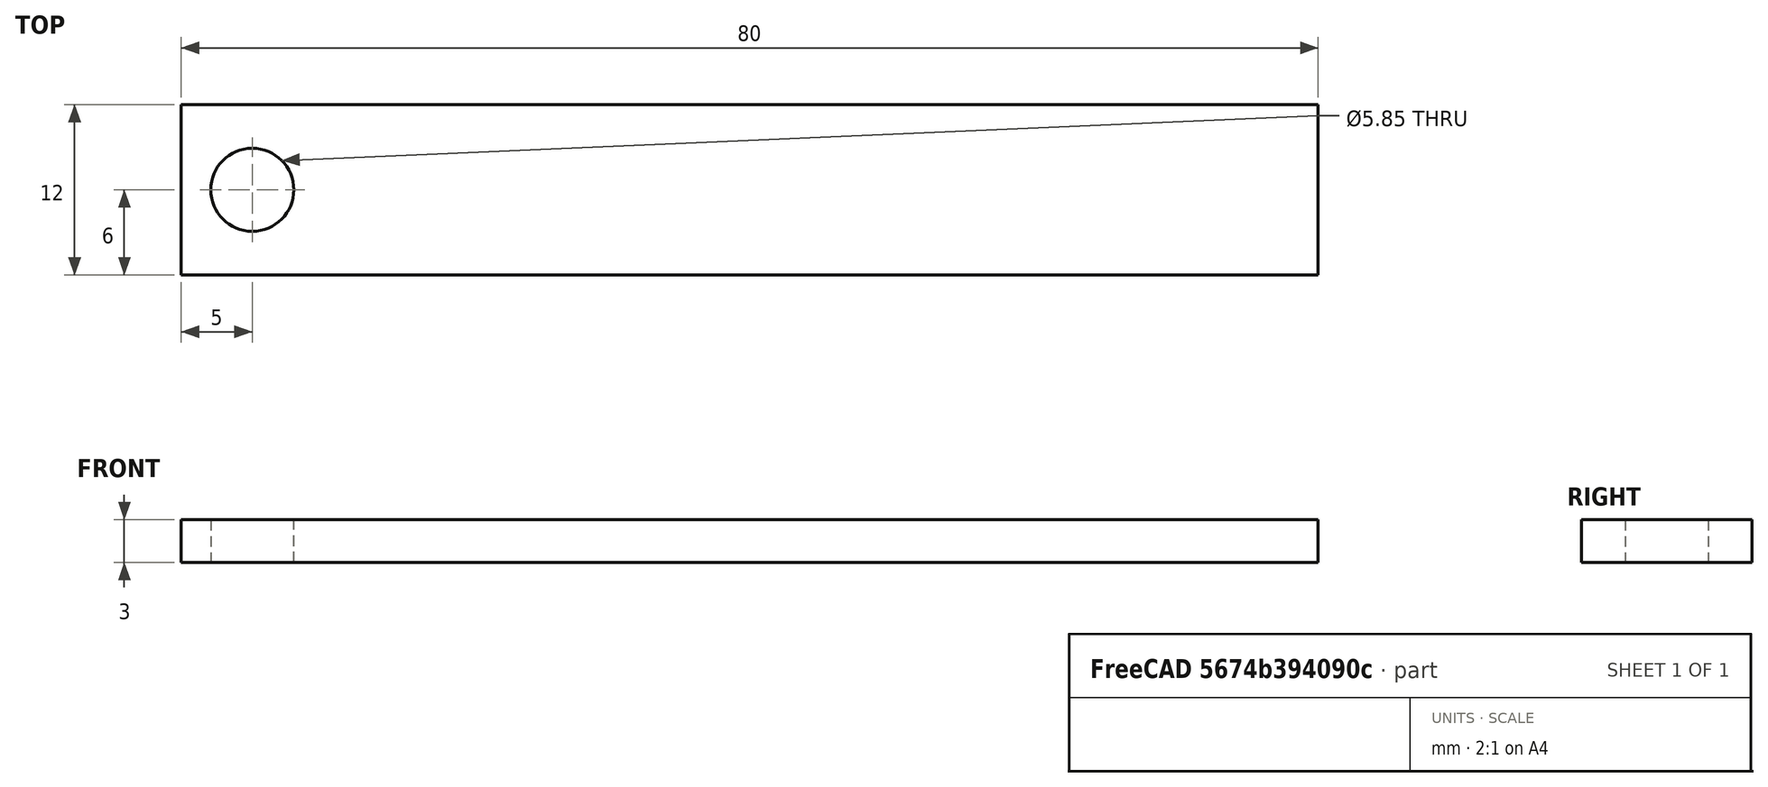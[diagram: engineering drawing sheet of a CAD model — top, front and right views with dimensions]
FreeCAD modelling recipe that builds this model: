
FCSTD DOCUMENT  (FreeCAD 1.0R39319 (Git))
Label: Rectangular_part
License: All rights reserved
LicenseURL: https://en.wikipedia.org/wiki/All_rights_reserved
objects: Sketcher::SketchObject×1, Part::Extrusion×1
note: 3 computed .brp shape members not serialized (recipe doc carries the construction recipe); baked Part::Feature solids carry a one-line shape summary decoded from their .brp

FEATURE [Sketcher::SketchObject] Sketch
  ArcFitTolerance = 1e-06
  FullyConstrained = false
  MakeInternals = false
  sketch-geometry (16):
    g0: LineSegment StartX=-40 StartY=-6 StartZ=0 EndX=40 EndY=-6 EndZ=0
    g1: LineSegment StartX=40 StartY=-6 StartZ=0 EndX=40 EndY=6 EndZ=0
    g2: LineSegment StartX=40 StartY=6 StartZ=0 EndX=-40 EndY=6 EndZ=0
    g3: LineSegment StartX=-40 StartY=6 StartZ=0 EndX=-40 EndY=-6 EndZ=0
    g4: GeomPoint [constr] X=0 Y=0 Z=0
    g5: Circle CenterX=-35 CenterY=0 CenterZ=0 NormalX=0 NormalY=0 NormalZ=1 AngleXU=0 Radius=2.92349
    g6: LineSegment StartX=22.9457 StartY=-42.794 StartZ=0 EndX=22.9457 EndY=42.794 EndZ=0
    g7: LineSegment StartX=22.9457 StartY=42.794 StartZ=0 EndX=-22.9457 EndY=42.794 EndZ=0
    g8: LineSegment StartX=-22.9457 StartY=42.794 StartZ=0 EndX=-22.9457 EndY=-42.794 EndZ=0
    g9: LineSegment StartX=-22.9457 StartY=-42.794 StartZ=0 EndX=22.9457 EndY=-42.794 EndZ=0
    g10: GeomPoint [constr] X=0 Y=0 Z=0
    g11: LineSegment StartX=22.9457 StartY=-42.794 StartZ=0 EndX=22.9457 EndY=42.794 EndZ=0
    g12: LineSegment StartX=22.9457 StartY=42.794 StartZ=0 EndX=-22.9457 EndY=42.794 EndZ=0
    g13: LineSegment StartX=-22.9457 StartY=42.794 StartZ=0 EndX=-22.9457 EndY=-42.794 EndZ=0
    g14: LineSegment StartX=-22.9457 StartY=-42.794 StartZ=0 EndX=22.9457 EndY=-42.794 EndZ=0
    g15: GeomPoint [constr] X=0 Y=0 Z=0
  constraints (38):
    c: Coincident(g0,g1)
    c: Coincident(g1,g2)
    c: Coincident(g2,g3)
    c: Coincident(g3,g0)
    c: Horizontal(g0)
    c: Horizontal(g2)
    c: Vertical(g1)
    c: Vertical(g3)
    c: Symmetric(g2,g0,g4)
    c: Distance(g1,g3) = 80
    c: Distance(g0,g2) = 12
    c: Coincident(g4,g-1)
    c: PointOnObject(g5,g-1)
    c: Distance(g5,g3) = 5
    c: Coincident(g0,g1)
    c: Coincident(g1,g2)
    c: Coincident(g2,g3)
    c: Coincident(g3,g0)
    c: Vertical(g0)
    c: Vertical(g2)
    c: Horizontal(g1)
    c: Horizontal(g3)
    c: Symmetric(g2,g0,g4)
    c: Coincident(g4,g-1)
    c: Distance(g2,g2) = 85.588
    c: DistanceY(g2,g2) = 85.588
    c: Coincident(g0,g1)
    c: Coincident(g1,g2)
    c: Coincident(g2,g3)
    c: Coincident(g3,g0)
    c: Vertical(g0)
    c: Vertical(g2)
    c: Horizontal(g1)
    c: Horizontal(g3)
    c: Symmetric(g2,g0,g4)
    c: Coincident(g4,g-1)
    c: Distance(g2,g2) = 85.588
    c: DistanceY(g2,g2) = 85.588
FEATURE [Part::Extrusion] Extrude
  Base = -> Sketch
  Dir = (0,0,1)
  DirMode = 2
  FaceMakerClass = Part::FaceMakerBullseye
  FaceMakerMode = 3
  LengthFwd = 3
  LengthRev = 0
  Solid = true
  Symmetric = false
